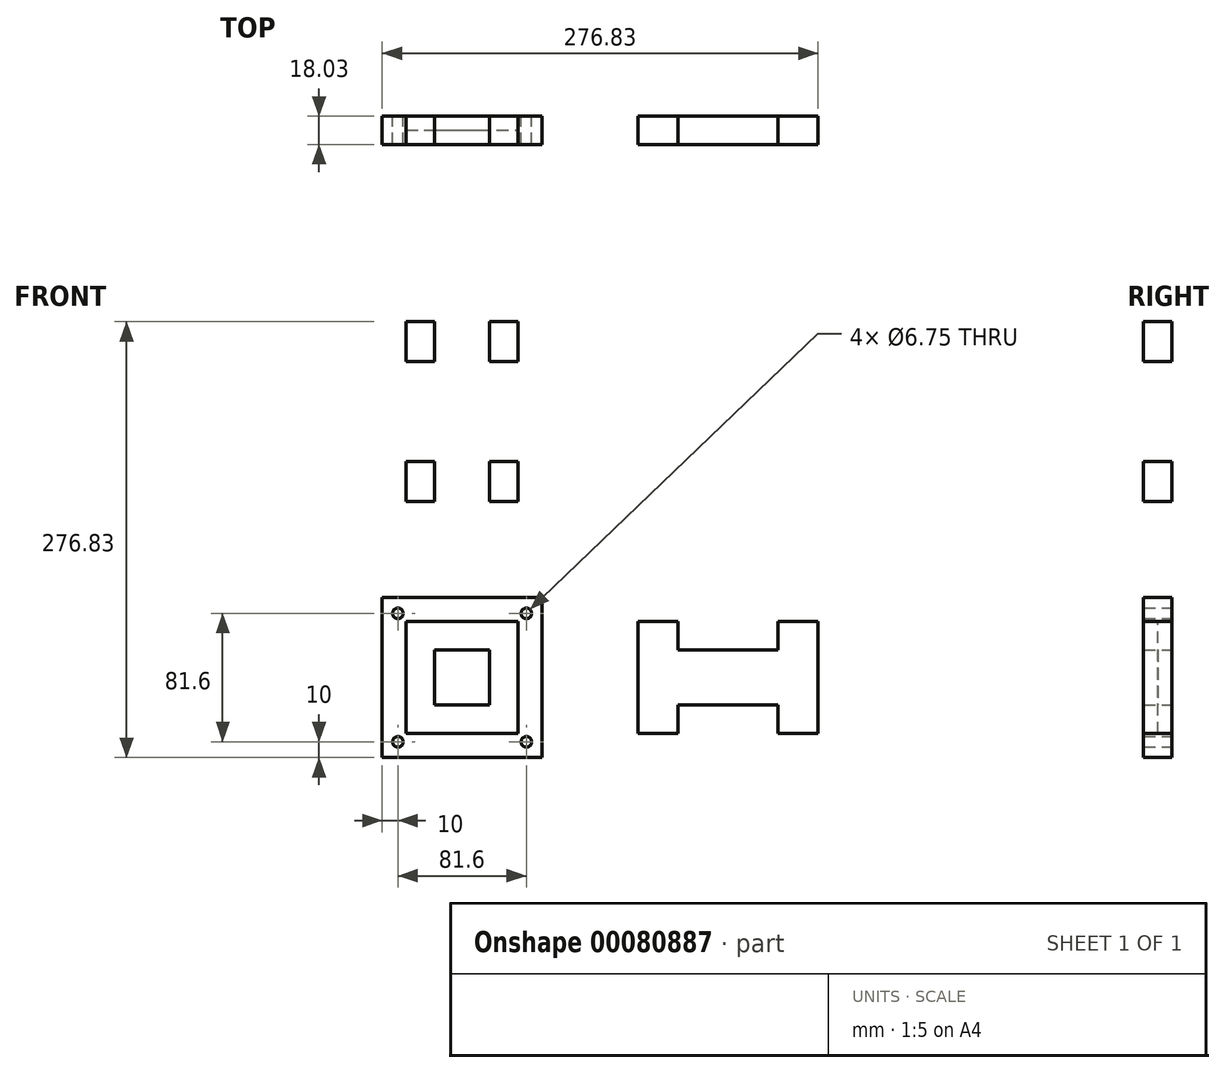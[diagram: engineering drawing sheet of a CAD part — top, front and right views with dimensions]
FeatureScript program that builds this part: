
annotation { "Feature Type Name" : "Feature", "Feature Type Description" : "" }
export const myFeature = defineFeature(function(context is Context, id is Id, definition is map)
    precondition{}
    {
        {
            var Q0;
            Q0=qCreatedBy(makeId("Front.planeOp"),FACE);
            var sketch = newSketch(context, id + "F0", { "sketchPlane" : qUnion([Q0])});
            skCircle(sketch, "E0", {"center": v(0, 0) * mm, "radius": 17.5 * mm});
            skLineSegment(sketch, "E1.bottom", {"start": v(-17.5, 17.5) * mm, "end": v(17.5, 17.5) * mm});
            skLineSegment(sketch, "E1.top", {"start": v(-17.5, -17.5) * mm, "end": v(17.5, -17.5) * mm});
            skLineSegment(sketch, "E1.left", {"start": v(-17.5, 17.5) * mm, "end": v(-17.5, -17.5) * mm});
            skLineSegment(sketch, "E1.right", {"start": v(17.5, 17.5) * mm, "end": v(17.5, -17.5) * mm});
            skLineSegment(sketch, "E2.bottom", {"start": v(-35.53, 17.5) * mm, "end": v(35.53, 17.5) * mm});
            skLineSegment(sketch, "E2.top", {"start": v(-35.53, 35.53) * mm, "end": v(35.53, 35.53) * mm});
            skLineSegment(sketch, "E2.left", {"start": v(-35.53, 17.5) * mm, "end": v(-35.53, 35.53) * mm});
            skLineSegment(sketch, "E2.right", {"start": v(35.53, 17.5) * mm, "end": v(35.53, 35.53) * mm});
            skPoint(sketch, "E3", {"position": v(0, 17.5) * mm});
            skLineSegment(sketch, "E4.bottom", {"start": v(35.53, -17.5) * mm, "end": v(-35.53, -17.5) * mm});
            skLineSegment(sketch, "E4.top", {"start": v(35.53, -35.53) * mm, "end": v(-35.53, -35.53) * mm});
            skLineSegment(sketch, "E4.left", {"start": v(35.53, -17.5) * mm, "end": v(35.53, -35.53) * mm});
            skLineSegment(sketch, "E4.right", {"start": v(-35.53, -17.5) * mm, "end": v(-35.53, -35.53) * mm});
            skLineSegment(sketch, "E5", {"start": v(-35.53, 17.5) * mm, "end": v(-35.53, -17.5) * mm});
            skLineSegment(sketch, "E6", {"start": v(35.53, 17.5) * mm, "end": v(35.53, -17.5) * mm});
            skLineSegment(sketch, "E7.bottom", {"start": v(-35.53, 111.73) * mm, "end": v(35.53, 111.73) * mm});
            skLineSegment(sketch, "E7.top", {"start": v(-35.53, 226.03) * mm, "end": v(35.53, 226.03) * mm});
            skLineSegment(sketch, "E7.left", {"start": v(-35.53, 111.73) * mm, "end": v(-35.53, 226.03) * mm});
            skLineSegment(sketch, "E7.right", {"start": v(35.53, 111.73) * mm, "end": v(35.53, 226.03) * mm});
            skLineSegment(sketch, "E8", {"start": v(0, 226.03) * mm, "end": v(0, 111.73) * mm, "construction": true});
            skLineSegment(sketch, "E9.bottom", {"start": v(111.73, 35.53) * mm, "end": v(226.03, 35.53) * mm});
            skLineSegment(sketch, "E9.top", {"start": v(111.73, -35.53) * mm, "end": v(226.03, -35.53) * mm});
            skLineSegment(sketch, "E9.left", {"start": v(111.73, 35.53) * mm, "end": v(111.73, -35.53) * mm});
            skLineSegment(sketch, "E9.right", {"start": v(226.03, 35.53) * mm, "end": v(226.03, -35.53) * mm});
            skPoint(sketch, "E9.middle", {"position": v(168.88, 0) * mm});
            skLineSegment(sketch, "E10.bottom", {"start": v(-50.8, 50.8) * mm, "end": v(50.8, 50.8) * mm});
            skLineSegment(sketch, "E10.top", {"start": v(-50.8, -50.8) * mm, "end": v(50.8, -50.8) * mm});
            skLineSegment(sketch, "E10.left", {"start": v(-50.8, 50.8) * mm, "end": v(-50.8, -50.8) * mm});
            skLineSegment(sketch, "E10.right", {"start": v(50.8, 50.8) * mm, "end": v(50.8, -50.8) * mm});
            skCircle(sketch, "E11", {"center": v(-40.8, 40.8) * mm, "radius": 3.37 * mm});
            skCircle(sketch, "E12.1.0", {"center": v(-40.8, -40.8) * mm, "radius": 3.37 * mm});
            skCircle(sketch, "E12.2.0", {"center": v(40.8, -40.8) * mm, "radius": 3.37 * mm});
            skCircle(sketch, "E12.3.0", {"center": v(40.8, 40.8) * mm, "radius": 3.37 * mm});
            skLineSegment(sketch, "E13.bottom", {"start": v(-35.53, 226.03) * mm, "end": v(-17.5, 226.03) * mm});
            skLineSegment(sketch, "E13.top", {"start": v(-35.53, 200.63) * mm, "end": v(-17.5, 200.63) * mm});
            skLineSegment(sketch, "E13.left", {"start": v(-35.53, 226.03) * mm, "end": v(-35.53, 200.63) * mm});
            skLineSegment(sketch, "E13.right", {"start": v(-17.5, 226.03) * mm, "end": v(-17.5, 200.63) * mm});
            skLineSegment(sketch, "E14", {"start": v(-35.53, 168.88) * mm, "end": v(35.53, 168.88) * mm, "construction": true});
            skLineSegment(sketch, "E15.MirrorCS", {"start": v(-35.53, 137.13) * mm, "end": v(-17.5, 137.13) * mm});
            skLineSegment(sketch, "E16.MirrorCS", {"start": v(-35.53, 111.73) * mm, "end": v(-35.53, 137.13) * mm});
            skLineSegment(sketch, "E17.MirrorCS", {"start": v(-17.5, 111.73) * mm, "end": v(-17.5, 137.13) * mm});
            skLineSegment(sketch, "E18.MirrorCS", {"start": v(-35.53, 111.73) * mm, "end": v(-17.5, 111.73) * mm});
            skLineSegment(sketch, "E19.MirrorCS", {"start": v(35.53, 226.03) * mm, "end": v(17.5, 226.03) * mm});
            skLineSegment(sketch, "E20.MirrorCS", {"start": v(17.5, 226.03) * mm, "end": v(17.5, 200.63) * mm});
            skLineSegment(sketch, "E21.MirrorCS", {"start": v(35.53, 200.63) * mm, "end": v(17.5, 200.63) * mm});
            skLineSegment(sketch, "E22.MirrorCS", {"start": v(35.53, 226.03) * mm, "end": v(35.53, 200.63) * mm});
            skLineSegment(sketch, "E23.MirrorCS", {"start": v(35.53, 111.73) * mm, "end": v(35.53, 137.13) * mm});
            skLineSegment(sketch, "E24.MirrorCS", {"start": v(17.5, 111.73) * mm, "end": v(17.5, 137.13) * mm});
            skLineSegment(sketch, "E25.MirrorCS", {"start": v(35.53, 137.13) * mm, "end": v(17.5, 137.13) * mm});
            skLineSegment(sketch, "E26.MirrorCS", {"start": v(35.53, 111.73) * mm, "end": v(17.5, 111.73) * mm});
            skLineSegment(sketch, "E27.bottom", {"start": v(137.13, 35.53) * mm, "end": v(200.63, 35.53) * mm});
            skLineSegment(sketch, "E27.top", {"start": v(137.13, 17.5) * mm, "end": v(200.63, 17.5) * mm});
            skLineSegment(sketch, "E27.left", {"start": v(137.13, 35.53) * mm, "end": v(137.13, 17.5) * mm});
            skLineSegment(sketch, "E27.right", {"start": v(200.63, 35.53) * mm, "end": v(200.63, 17.5) * mm});
            skLineSegment(sketch, "E28", {"start": v(111.73, 0) * mm, "end": v(226.03, 0) * mm, "construction": true});
            skLineSegment(sketch, "E29.MirrorCS", {"start": v(200.63, -35.53) * mm, "end": v(200.63, -17.5) * mm});
            skLineSegment(sketch, "E30.MirrorCS", {"start": v(137.13, -35.53) * mm, "end": v(200.63, -35.53) * mm});
            skLineSegment(sketch, "E31.MirrorCS", {"start": v(137.13, -35.53) * mm, "end": v(137.13, -17.5) * mm});
            skLineSegment(sketch, "E32.MirrorCS", {"start": v(137.13, -17.5) * mm, "end": v(200.63, -17.5) * mm});
            skCircle(sketch, "E33", {"center": v(-203.2, 0) * mm, "radius": 50.55 * mm});
            skPoint(sketch, "E33.centerSnap0", {"position": v(-50.8, 0) * mm});
            skCircle(sketch, "E34", {"center": v(-203.2, 0) * mm, "radius": 4.83 * mm});
            skSolve(sketch);
        }
        {
            var Q0;
            {var subQ0=sQuery(id+"F0.wireOp",EDGE,"Y1KIgJUp-MOgn-eK3c-SsGM-PXHpgYowiuGM");Q0=makeQuery(id+"F0.imprint","IMPRINT",FACE,{"disambiguationData":[TD([[makeQuery(id+"F0.imprint","IMPRINT",EDGE,{"derivedFrom":subQ0}),-1.0]])]});}
            var Q1;
            {var subQ0=sQuery(id+"F0.wireOp",EDGE,"E7.left");Q1=makeQuery(id+"F0.imprint","IMPRINT",FACE,{"disambiguationData":[TD([[makeQuery(id+"F0.imprint","IMPRINT",EDGE,{"derivedFrom":subQ0}),-1.0]])]});}
            var Q2;
            {var subQ0=sQuery(id+"F0.wireOp",EDGE,"E7.right");Q2=makeQuery(id+"F0.imprint","IMPRINT",FACE,{"disambiguationData":[TD([[makeQuery(id+"F0.imprint","IMPRINT",EDGE,{"derivedFrom":subQ0}),1.0]])]});}
            var Q3;
            {var subQ0=sQuery(id+"F0.wireOp",EDGE,"RKQd7QR6-2gtZ-n0R2-ziLU-ey0x4MDIaPKX");Q3=makeQuery(id+"F0.imprint","IMPRINT",FACE,{"disambiguationData":[TD([[makeQuery(id+"F0.imprint","IMPRINT",EDGE,{"derivedFrom":subQ0}),-1.0]])]});}
            var Q4;
            Q4=makeQuery(id+"F0.imprint","IMPRINT",FACE,{"disambiguationData":[TD([[makeQuery(id+"F0.imprint","IMPRINT",EDGE,{"derivedFrom":sQuery(id+"F0.wireOp",EDGE,"E2.top")}),1.0]])]});
            var Q5;
            {var subQ0=sQuery(id+"F0.wireOp",EDGE,"E2.bottom");var subQ1=sQuery(id+"F0.wireOp",EDGE,"E0");var subQ2=makeQuery(id+"F0.imprint","INTERSECT",VERTEX,{"derivedFrom":[subQ1,subQ0]});Q5=makeQuery(id+"F0.imprint","IMPRINT",FACE,{"disambiguationData":[TD([[makeQuery(id+"F0.imprint","IMPRINT",EDGE,{"disambiguationData":[TD([[subQ2,1.0]])],"derivedFrom":subQ1}),-1.0]])]});}
            var Q6;
            {var subQ0=sQuery(id+"F0.wireOp",EDGE,"E2.bottom");var subQ1=sQuery(id+"F0.wireOp",EDGE,"E0");var subQ2=makeQuery(id+"F0.imprint","INTERSECT",VERTEX,{"derivedFrom":[subQ1,subQ0]});Q6=makeQuery(id+"F0.imprint","IMPRINT",FACE,{"disambiguationData":[TD([[makeQuery(id+"F0.imprint","IMPRINT",EDGE,{"disambiguationData":[TD([[subQ2,-1.0]])],"derivedFrom":subQ1}),-1.0]])]});}
            var Q7;
            {var subQ0=sQuery(id+"F0.wireOp",EDGE,"E0");var subQ1=makeQuery(id+"F0.imprint","INTERSECT",VERTEX,{"derivedFrom":[subQ0,sQuery(id+"F0.wireOp",EDGE,"E2.bottom")]});Q7=makeQuery(id+"F0.imprint","IMPRINT",FACE,{"disambiguationData":[TD([[makeQuery(id+"F0.imprint","IMPRINT",EDGE,{"disambiguationData":[TD([[subQ1,1.0]])],"derivedFrom":subQ0}),1.0]])]});}
            var Q8;
            {var subQ0=sQuery(id+"F0.wireOp",EDGE,"E1.left");var subQ1=sQuery(id+"F0.wireOp",EDGE,"E0");var subQ2=makeQuery(id+"F0.imprint","INTERSECT",VERTEX,{"derivedFrom":[subQ1,subQ0]});Q8=makeQuery(id+"F0.imprint","IMPRINT",FACE,{"disambiguationData":[TD([[makeQuery(id+"F0.imprint","IMPRINT",EDGE,{"disambiguationData":[TD([[subQ2,-1.0]])],"derivedFrom":subQ1}),-1.0]])]});}
            var Q9;
            {var subQ0=sQuery(id+"F0.wireOp",EDGE,"E1.right");var subQ1=sQuery(id+"F0.wireOp",EDGE,"E0");var subQ2=makeQuery(id+"F0.imprint","INTERSECT",VERTEX,{"derivedFrom":[subQ1,subQ0]});Q9=makeQuery(id+"F0.imprint","IMPRINT",FACE,{"disambiguationData":[TD([[makeQuery(id+"F0.imprint","IMPRINT",EDGE,{"disambiguationData":[TD([[subQ2,1.0]])],"derivedFrom":subQ1}),-1.0]])]});}
            var Q10;
            {var subQ1=sQuery(id+"F0.wireOp",EDGE,"E9.left");Q10=makeQuery(id+"F0.imprint","IMPRINT",FACE,{"disambiguationData":[TD([[makeQuery(id+"F0.imprint","IMPRINT",EDGE,{"derivedFrom":subQ1}),1.0]])]});}
            extrude(context, id + "F1", {"entities" : qUnion([Q0, Q1, Q2, Q3, Q4, Q5, Q6, Q7, Q8, Q9, Q10]), "depth" : 18.03 * mm});
        }
        {
            var Q0;
            {var subQ0=sQuery(id+"F0.wireOp",EDGE,"Y1KIgJUp-MOgn-eK3c-SsGM-PXHpgYowiuGM");Q0=makeQuery(id+"F0.imprint","IMPRINT",FACE,{"disambiguationData":[TD([[makeQuery(id+"F0.imprint","IMPRINT",EDGE,{"derivedFrom":subQ0}),1.0]])]});}
            var Q1;
            {var subQ0=sQuery(id+"F0.wireOp",EDGE,"e188e6ec-3e99-4ba3-af61-ec22c907ed7a0.MirrorCS");Q1=makeQuery(id+"F0.imprint","IMPRINT",FACE,{"disambiguationData":[TD([[makeQuery(id+"F0.imprint","IMPRINT",EDGE,{"derivedFrom":subQ0}),1.0]])]});}
            var Q2;
            Q2=makeQuery(id+"F0.imprint","IMPRINT",FACE,{"disambiguationData":[TD([[makeQuery(id+"F0.imprint","IMPRINT",EDGE,{"derivedFrom":sQuery(id+"F0.wireOp",EDGE,"E2.top")}),-1.0]])]});
            var Q3;
            {var subQ3=sQuery(id+"F0.wireOp",EDGE,"E5");Q3=makeQuery(id+"F0.imprint","IMPRINT",FACE,{"disambiguationData":[TD([[makeQuery(id+"F0.imprint","IMPRINT",EDGE,{"derivedFrom":subQ3}),1.0]])]});}
            var Q4;
            Q4=makeQuery(id+"F0.imprint","IMPRINT",FACE,{"disambiguationData":[TD([[makeQuery(id+"F0.imprint","IMPRINT",EDGE,{"derivedFrom":sQuery(id+"F0.wireOp",EDGE,"E4.top")}),-1.0]])]});
            var Q5;
            {var subQ3=sQuery(id+"F0.wireOp",EDGE,"E6");Q5=makeQuery(id+"F0.imprint","IMPRINT",FACE,{"disambiguationData":[TD([[makeQuery(id+"F0.imprint","IMPRINT",EDGE,{"derivedFrom":subQ3}),-1.0]])]});}
            extrude(context, id + "F2", {"entities" : qUnion([Q0, Q1, Q2, Q3, Q4, Q5]), "operationType" : NewBodyOperationType.ADD, "depth" : 8.9 * mm});
        }
    });
